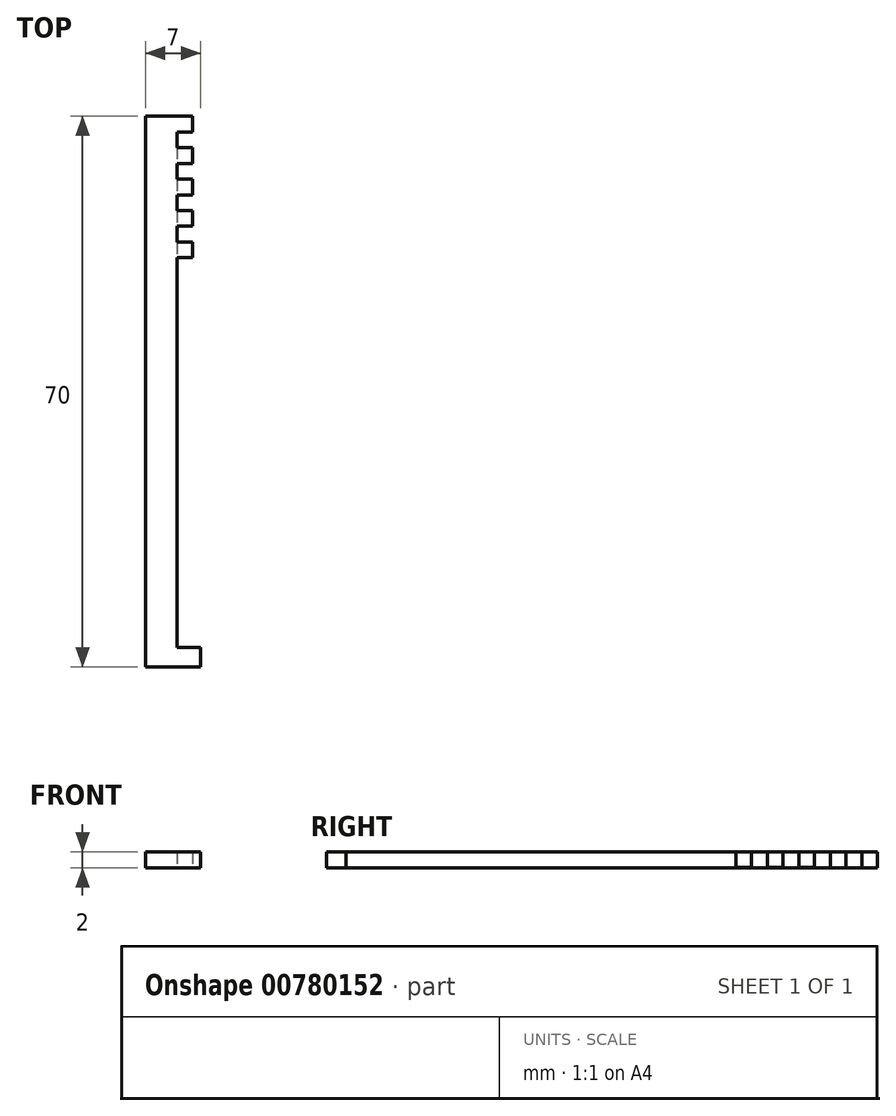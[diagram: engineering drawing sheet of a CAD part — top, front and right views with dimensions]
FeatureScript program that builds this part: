
annotation { "Feature Type Name" : "Feature", "Feature Type Description" : "" }
export const myFeature = defineFeature(function(context is Context, id is Id, definition is map)
    precondition{}
    {
        {
            var Q0;
            Q0=qCreatedBy(makeId("Top.planeOp"),FACE);
            var sketch = newSketch(context, id + "F0", { "sketchPlane" : qUnion([Q0])});
            skLineSegment(sketch, "E0", {"start": v(-2, 35) * mm, "end": v(-2, -35) * mm});
            skLineSegment(sketch, "E1", {"start": v(-2, -35) * mm, "end": v(5, -35) * mm});
            skLineSegment(sketch, "E2", {"start": v(5, -35) * mm, "end": v(5, -32.5) * mm});
            skLineSegment(sketch, "E3", {"start": v(5, -32.5) * mm, "end": v(2, -32.5) * mm});
            skLineSegment(sketch, "E4", {"start": v(2, -32.5) * mm, "end": v(2, 35) * mm});
            skLineSegment(sketch, "E5", {"start": v(2, 35) * mm, "end": v(-2, 35) * mm});
            skSolve(sketch);
        }
        {
            var Q0;
            Q0=makeQuery(id+"F0.imprint","IMPRINT",FACE,{"disambiguationData":[TD([[makeQuery(id+"F0.imprint","IMPRINT",EDGE,{"derivedFrom":sQuery(id+"F0.wireOp",EDGE,"E0")}),1.0]])]});
            extrude(context, id + "F1", {"entities" : qUnion([Q0]), "depth" : 2 * mm, "offsetDistance" : 25 * mm});
        }
        {
            var Q0;
            Q0=makeQuery(id+"F1.opExtrude","SWEPT_FACE",FACE,{"disambiguationData":[OSD([sQuery(id+"F0.wireOp",EDGE,"E4")])]});
            var sketch = newSketch(context, id + "F2", { "sketchPlane" : qUnion([Q0])});
            skLineSegment(sketch, "E6.bottom", {"start": v(35, 2) * mm, "end": v(33, 2) * mm});
            skLineSegment(sketch, "E6.top", {"start": v(35, 0) * mm, "end": v(33, 0) * mm});
            skLineSegment(sketch, "E6.left", {"start": v(35, 2) * mm, "end": v(35, 0) * mm});
            skLineSegment(sketch, "E6.right", {"start": v(33, 2) * mm, "end": v(33, 0) * mm});
            skLineSegment(sketch, "E7.1.0.0", {"start": v(31, 2.02) * mm, "end": v(29, 2.02) * mm});
            skLineSegment(sketch, "E7.1.0.1", {"start": v(31, 0.02) * mm, "end": v(29, 0.02) * mm});
            skLineSegment(sketch, "E7.1.0.2", {"start": v(31, 2.02) * mm, "end": v(31, 0.02) * mm});
            skLineSegment(sketch, "E7.1.0.3", {"start": v(29, 2.02) * mm, "end": v(29, 0.02) * mm});
            skLineSegment(sketch, "E7.2.0.0", {"start": v(27, 2.03) * mm, "end": v(25, 2.03) * mm});
            skLineSegment(sketch, "E7.2.0.1", {"start": v(27, 0.03) * mm, "end": v(25, 0.03) * mm});
            skLineSegment(sketch, "E7.2.0.2", {"start": v(27, 2.03) * mm, "end": v(27, 0.03) * mm});
            skLineSegment(sketch, "E7.2.0.3", {"start": v(25, 2.03) * mm, "end": v(25, 0.03) * mm});
            skLineSegment(sketch, "E7.3.0.0", {"start": v(23, 2.05) * mm, "end": v(21, 2.05) * mm});
            skLineSegment(sketch, "E7.3.0.1", {"start": v(23, 0.05) * mm, "end": v(21, 0.05) * mm});
            skLineSegment(sketch, "E7.3.0.2", {"start": v(23, 2.05) * mm, "end": v(23, 0.05) * mm});
            skLineSegment(sketch, "E7.3.0.3", {"start": v(21, 2.05) * mm, "end": v(21, 0.05) * mm});
            skLineSegment(sketch, "E7.4.0.0", {"start": v(19, 2.07) * mm, "end": v(17, 2.07) * mm});
            skLineSegment(sketch, "E7.4.0.1", {"start": v(19, 0.07) * mm, "end": v(17, 0.07) * mm});
            skLineSegment(sketch, "E7.4.0.2", {"start": v(19, 2.07) * mm, "end": v(19, 0.07) * mm});
            skLineSegment(sketch, "E7.4.0.3", {"start": v(17, 2.07) * mm, "end": v(17, 0.07) * mm});
            skLineSegment(sketch, "E7.direction1", {"start": v(33, 2) * mm, "end": v(29, 2.02) * mm, "construction": true});
            skSolve(sketch);
        }
        {
            var Q0;
            Q0=makeQuery(id+"F2.imprint","IMPRINT",FACE,{"disambiguationData":[TD([[makeQuery(id+"F2.imprint","IMPRINT",EDGE,{"derivedFrom":sQuery(id+"F2.wireOp",EDGE,"E6.bottom")}),-1.0]])]});
            var Q1;
            {var subQ0=sQuery(id+"F2.wireOp",EDGE,"E7.1.0.1");Q1=makeQuery(id+"F2.imprint","IMPRINT",FACE,{"disambiguationData":[TD([[makeQuery(id+"F2.imprint","IMPRINT",EDGE,{"derivedFrom":subQ0}),-1.0]])]});}
            var Q2;
            {var subQ0=sQuery(id+"F2.wireOp",EDGE,"E7.2.0.1");Q2=makeQuery(id+"F2.imprint","IMPRINT",FACE,{"disambiguationData":[TD([[makeQuery(id+"F2.imprint","IMPRINT",EDGE,{"derivedFrom":subQ0}),-1.0]])]});}
            var Q3;
            {var subQ0=sQuery(id+"F2.wireOp",EDGE,"E7.3.0.1");Q3=makeQuery(id+"F2.imprint","IMPRINT",FACE,{"disambiguationData":[TD([[makeQuery(id+"F2.imprint","IMPRINT",EDGE,{"derivedFrom":subQ0}),-1.0]])]});}
            var Q4;
            {var subQ0=sQuery(id+"F2.wireOp",EDGE,"E7.4.0.1");Q4=makeQuery(id+"F2.imprint","IMPRINT",FACE,{"disambiguationData":[TD([[makeQuery(id+"F2.imprint","IMPRINT",EDGE,{"derivedFrom":subQ0}),-1.0]])]});}
            extrude(context, id + "F3", {"entities" : qUnion([Q0, Q1, Q2, Q3, Q4]), "operationType" : NewBodyOperationType.ADD, "depth" : 2 * mm, "offsetDistance" : 25 * mm});
        }
    });
